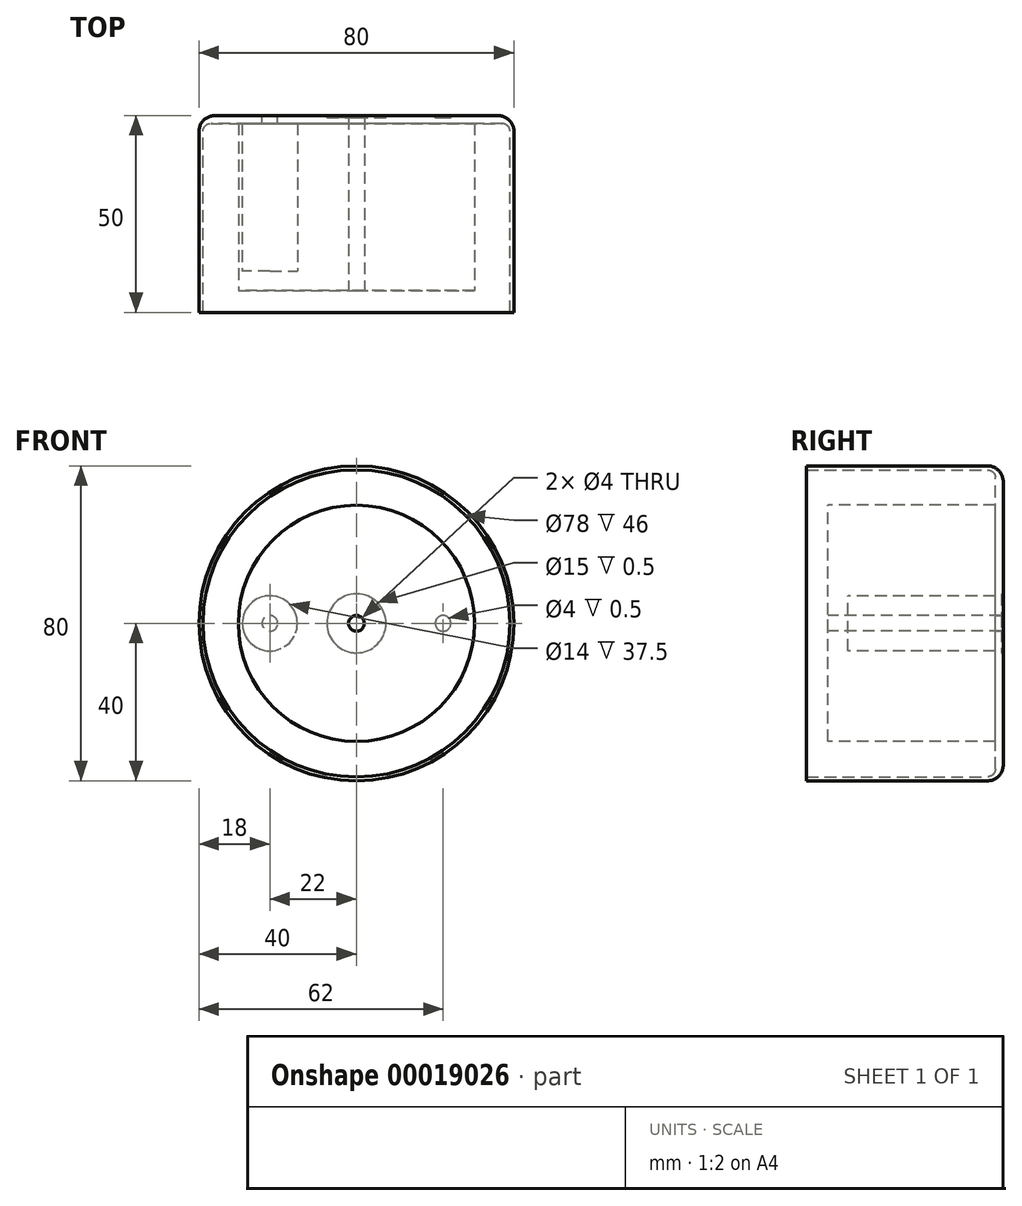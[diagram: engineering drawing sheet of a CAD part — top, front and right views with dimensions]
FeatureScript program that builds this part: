
annotation { "Feature Type Name" : "Feature", "Feature Type Description" : "" }
export const myFeature = defineFeature(function(context is Context, id is Id, definition is map)
    precondition{}
    {
        {
            var Q0;
            Q0=qCreatedBy(makeId("Front.planeOp"),FACE);
            var sketch = newSketch(context, id + "F0", { "sketchPlane" : qUnion([Q0])});
            skCircle(sketch, "E0", {"center": v(0, 0) * mm, "radius": 40 * mm});
            skCircle(sketch, "E1", {"center": v(0, 0) * mm, "radius": 39 * mm});
            skSolve(sketch);
        }
        {
            var Q0;
            Q0=makeQuery(id+"F0.imprint","IMPRINT",FACE,{"disambiguationData":[TD([[makeQuery(id+"F0.imprint","IMPRINT",EDGE,{"derivedFrom":sQuery(id+"F0.wireOp",EDGE,"E0")}),1.0]])]});
            extrude(context, id + "F1", {"entities" : qUnion([Q0]), "depth" : 50 * mm});
        }
        {
            var Q0;
            Q0=qCreatedBy(makeId("Front.planeOp"),FACE);
            var sketch = newSketch(context, id + "F2", { "sketchPlane" : qUnion([Q0])});
            skCircle(sketch, "E2.0", {"center": v(0, 0) * mm, "radius": 40 * mm});
            skCircle(sketch, "E3", {"center": v(0, 0) * mm, "radius": 7.5 * mm});
            skCircle(sketch, "E4", {"center": v(-22, 0) * mm, "radius": 2 * mm});
            skCircle(sketch, "E5.MirrorC", {"center": v(22, 0) * mm, "radius": 2 * mm});
            skSolve(sketch);
        }
        {
            var Q0;
            Q0 = qSketchRegion(id + "F2", true);
            extrude(context, id + "F3", {"entities" : qUnion([Q0]), "operationType" : NewBodyOperationType.ADD, "depth" : 2 * mm});
        }
        {
            var Q0;
            Q0=makeQuery(id+"F3.boolean.opBoolean","INTERSECT",EDGE,{"derivedFrom":[makeQuery(id+"F1.opExtrude","SWEPT_FACE",FACE,{"disambiguationData":[OSD([sQuery(id+"F0.wireOp",EDGE,"E1")])]}),makeQuery(id+"F3.opExtrude","CAP_FACE",FACE,{"disambiguationData":[OSD([sQuery(id+"F2.wireOp",EDGE,"E2.0"),sQuery(id+"F2.wireOp",EDGE,"E3"),sQuery(id+"F2.wireOp",EDGE,"E4"),sQuery(id+"F2.wireOp",EDGE,"E5.MirrorC")])],"isStart":false})]});
            fillet(context, id + "F4", {"entities" : qUnion([Q0]), "radius" : 2 * mm, "tangentPropagation" : true, "allowEdgeOverflow" : false});
        }
        {
            var Q0;
            Q0=makeQuery(id+"F1.opExtrude","CAP_EDGE",EDGE,{"disambiguationData":[OSD([sQuery(id+"F0.wireOp",EDGE,"E0")])],"isStart":true});
            fillet(context, id + "F5", {"entities" : qUnion([Q0]), "radius" : 4 * mm, "tangentPropagation" : true, "allowEdgeOverflow" : false});
        }
        {
            var Q0;
            Q0=qCreatedBy(makeId("Front.planeOp"),FACE);
            cPlane(context, id + "F6", {"entities" : qUnion([Q0]), "cplaneType" : CPlaneType.OFFSET, "offset" : 44.5 * mm, "width" : 150 * mm, "height" : 150 * mm});
        }
        {
            var Q0;
            Q0=qCreatedBy(id+"F6.planeOp",FACE);
            var sketch = newSketch(context, id + "F7", { "sketchPlane" : qUnion([Q0])});
            skCircle(sketch, "E6", {"center": v(0, 0) * mm, "radius": 30 * mm});
            skPoint(sketch, "E7", {"position": v(-10.5, 0) * mm});
            skPoint(sketch, "E8.MirrorP", {"position": v(10.5, 0) * mm});
            skCircle(sketch, "E9", {"center": v(0, 0) * mm, "radius": 2 * mm});
            skSolve(sketch);
        }
        {
            var Q0;
            Q0=makeQuery(id+"F7.imprint","IMPRINT",FACE,{"disambiguationData":[TD([[makeQuery(id+"F7.imprint","IMPRINT",EDGE,{"derivedFrom":sQuery(id+"F7.wireOp",EDGE,"E6")}),1.0]])]});
            extrude(context, id + "F8", {"entities" : qUnion([Q0]), "oppositeDirection" : true, "depth" : 5 * mm});
        }
        {
            var Q0;
            Q0=makeQuery(id+"F8.opExtrude","CAP_FACE",FACE,{"disambiguationData":[OSD([sQuery(id+"F7.wireOp",EDGE,"E6"),sQuery(id+"F7.wireOp",EDGE,"E9")])],"isStart":false});
            var sketch = newSketch(context, id + "F9", { "sketchPlane" : qUnion([Q0])});
            skPoint(sketch, "E10.0", {"position": v(-22, 0) * mm});
            skCircle(sketch, "E11", {"center": v(-22, 0) * mm, "radius": 7 * mm});
            skCircle(sketch, "E12", {"center": v(0, -6) * mm, "radius": 15 * mm, "construction": true});
            skCircle(sketch, "E13.MirrorC", {"center": v(22, 0) * mm, "radius": 7 * mm});
            skSolve(sketch);
        }
        {
            var Q0;
            Q0=makeQuery(id+"F9.imprint","IMPRINT",FACE,{"disambiguationData":[TD([[makeQuery(id+"F9.imprint","IMPRINT",EDGE,{"derivedFrom":sQuery(id+"F9.wireOp",EDGE,"E11")}),1.0]])]});
            extrude(context, id + "F10", {"entities" : qUnion([Q0]), "operationType" : NewBodyOperationType.ADD, "depth" : 39 * mm});
        }
        {
            var Q0;
            Q0=makeQuery(id+"F9.imprint","IMPRINT",FACE,{"disambiguationData":[TD([[makeQuery(id+"F9.imprint","IMPRINT",EDGE,{"derivedFrom":sQuery(id+"F9.wireOp",EDGE,"E13.MirrorC")}),-1.0]])]});
            extrude(context, id + "F11", {"entities" : qUnion([Q0]), "operationType" : NewBodyOperationType.ADD, "depth" : 39 * mm});
        }
    });
